# Revit family: Kessel 93010.32DS en
name_source: partatom
category: Plumbing Fixtures
revit_build: Autodesk Revit Architecture 2014 (Build: 20130308_1515(x64)
units: mm (PartAtom-declared; Revit-internal decimal feet)

## types (1)
- Kessel 93010.32DS en
    <1.010.00.2> Number of the part of the guideline = 98
    <1.010.00.3> Issue date (month) of the guideline = 200601
    <1.010.00.4> Manufacturer name = Kessel
    <1.010.00.5> Revision date of the file = 20190227
    <1.800.00.3> BS number = 001001000001004005004001001002002002005???00700062???
    <1.800.00.4> Comment field = EasyClean free grease separator, NS 10, Mix, inspection window, SonicControl
    <1.810.00.3> Manufacturer’s reference number = 93010.32/DS
    <1.810.00.4> DATANORM number = 93010.32/DS
    <1.810.00.6> GTIN number = 4026092068946
    <1.960/3L.00.8> Link (URL) = http://www.kessel.de
    <98.100.00.4> Area of application = Grease separator
    <98.110.00.4> Product series = EasyClean free grease separator
    <98.200.00.3> Installation of the separators (DIN 19901) = Freestanding
    <98.250.00.3> Disposal variant = Mix
    <98.260.00.3> Sludge trap content (liters) = 1000
    <98.300.00.3> Separator content (liters) = 900
    <98.350.00.3> Fat storage (liters) = 400
    <98.360.00.3> Total volume (liters) = 1900
    <98.400.00.3> Layer thickness measurement (SonicControl) = yes
    <98.450.00.3> Inlet nominal diameter (DN) = 150
    <98.460.00.3> Outlet nominal diameter (DN) = 150
    <98.500.00.3> Nominal size (NS) = 10
    <98.700.00.4> Product name = EasyClean free grease separator, NS 10, Mix, inspection window, SonicControl
    CONNECTOR0_DIAMETER_dX_0r = 0 mm  [stored 0 ft]
    CONNECTOR0_dX_00 = 1440 mm
    CONNECTOR0_dX_01 = 1360 mm
    CONNECTOR0_ref_dX = 1360 mm
    CONNECTOR0_ref_dZ = 1336 mm
    CONNECTOR1_DIAMETER_dZ_0r = 0 mm  [stored 0 ft]
    CONNECTOR1_dZ_00 = 1928 mm
    CONNECTOR1_dZ_01 = 1938 mm
    CONNECTOR1_ref_dX = 305 mm  [stored 1.00066 ft]
    CONNECTOR1_ref_dY = 374 mm  [stored 1.22703 ft]
    CONNECTOR1_ref_dZ = 1928 mm
    CONNECTOR2_DIAMETER_dZ_0r = 0 mm  [stored 0 ft]
    CONNECTOR2_dZ_00 = 239 mm
    CONNECTOR2_dZ_01 = 249 mm
    CONNECTOR2_ref_dX = 212 mm
    CONNECTOR2_ref_dY = 515 mm
    CONNECTOR2_ref_dZ = 239 mm
    CONNECTOR3_DIAMETER_dX_0r = 0 mm  [stored 0 ft]
    CONNECTOR3_dX_00 = 1307 mm
    CONNECTOR3_dX_01 = 1387 mm
    CONNECTOR3_ref_dX = 1307 mm
    CONNECTOR3_ref_dZ = 1265 mm
    CONNECTOR4_DIAMETER_dZ_0r = 0 mm  [stored 0 ft]
    CONNECTOR4_dZ_00 = 1350 mm
    CONNECTOR4_dZ_01 = 1430 mm
    CONNECTOR4_ref_dX = 290 mm
    CONNECTOR4_ref_dY = 435 mm
    CONNECTOR4_ref_dZ = 1350 mm
    Manufacturer = Kessel
    Model = 93010.32/DS
    URL = www.kessel.com

note: [stored X ft] marks values corroborated as IEEE doubles in the binary element streams (Revit-internal decimal feet)
